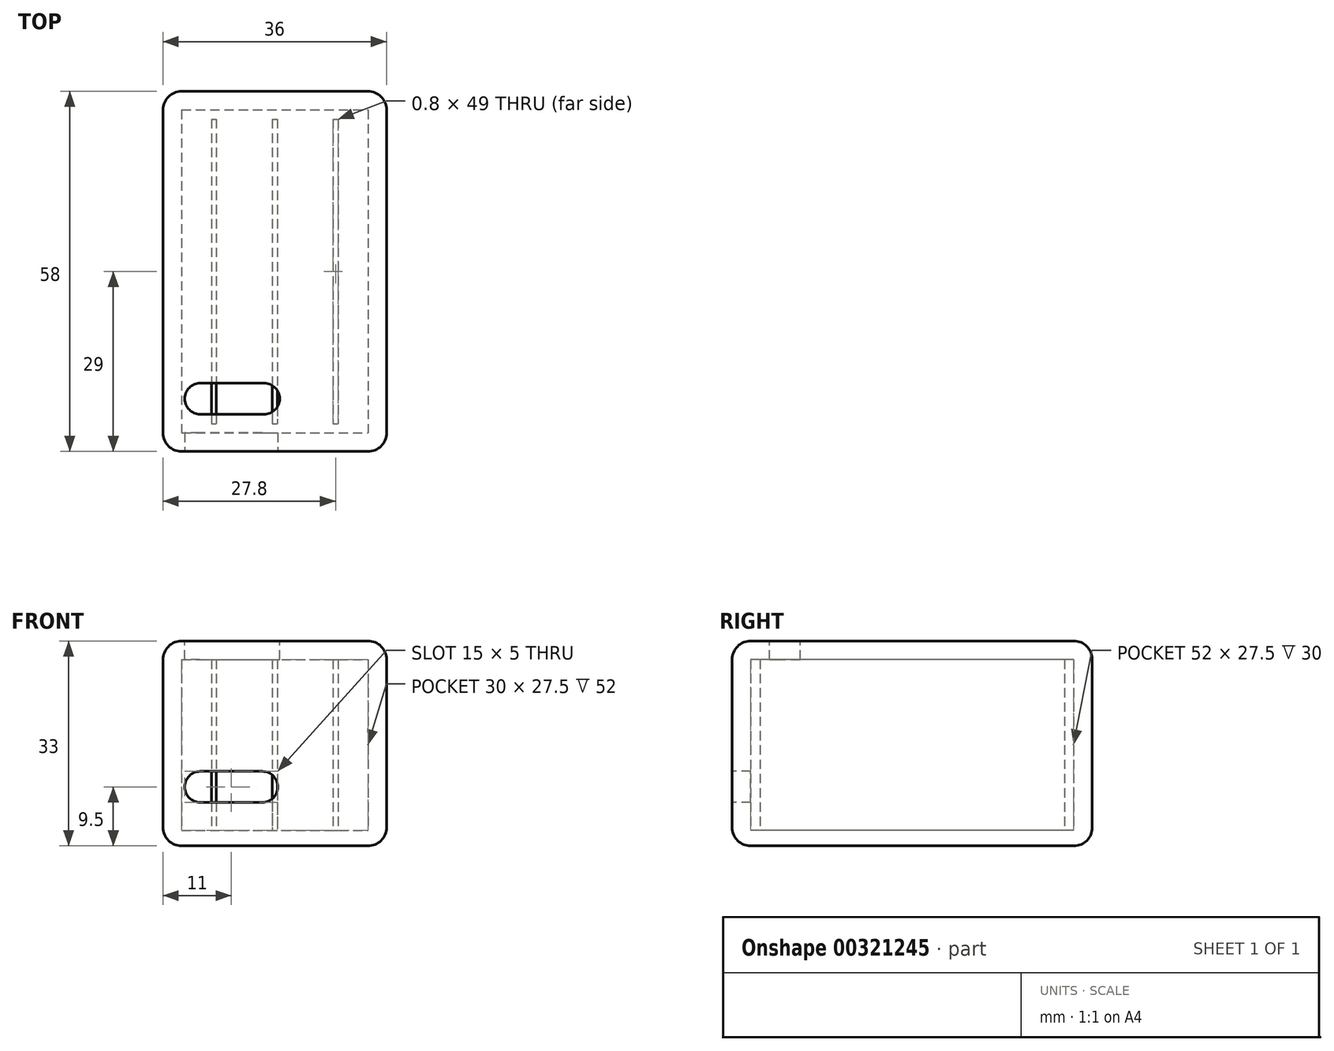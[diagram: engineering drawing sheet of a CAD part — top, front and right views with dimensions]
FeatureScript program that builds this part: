
annotation { "Feature Type Name" : "Feature", "Feature Type Description" : "" }
export const myFeature = defineFeature(function(context is Context, id is Id, definition is map)
    precondition{}
    {
        {
            var Q0;
            Q0=qCreatedBy(makeId("Top.planeOp"),FACE);
            var sketch = newSketch(context, id + "F0", { "sketchPlane" : qUnion([Q0])});
            skLineSegment(sketch, "E0.bottom", {"start": v(-15, 26) * mm, "end": v(15, 26) * mm});
            skLineSegment(sketch, "E0.top", {"start": v(-15, -26) * mm, "end": v(15, -26) * mm});
            skLineSegment(sketch, "E0.left", {"start": v(-15, 26) * mm, "end": v(-15, -26) * mm});
            skLineSegment(sketch, "E0.right", {"start": v(15, 26) * mm, "end": v(15, -26) * mm});
            skPoint(sketch, "E1", {"position": v(-15, 0) * mm});
            skPoint(sketch, "E2", {"position": v(0, 26) * mm});
            skLineSegment(sketch, "E3.bottom", {"start": v(-18, 29) * mm, "end": v(18, 29) * mm});
            skLineSegment(sketch, "E3.top", {"start": v(-18, -29) * mm, "end": v(18, -29) * mm});
            skLineSegment(sketch, "E3.left", {"start": v(-18, 29) * mm, "end": v(-18, -29) * mm});
            skLineSegment(sketch, "E3.right", {"start": v(18, 29) * mm, "end": v(18, -29) * mm});
            skPoint(sketch, "E4", {"position": v(-18, 0) * mm});
            skPoint(sketch, "E5", {"position": v(0, 29) * mm});
            skSolve(sketch);
        }
        {
            var Q0;
            Q0 = qSketchRegion(id + "F0", true);
            extrude(context, id + "F1", {"entities" : qUnion([Q0]), "depth" : 30 * mm});
        }
        {
            var Q0;
            Q0=makeQuery(id+"F0.imprint","IMPRINT",FACE,{"disambiguationData":[TD([[makeQuery(id+"F0.imprint","IMPRINT",EDGE,{"derivedFrom":sQuery(id+"F0.wireOp",EDGE,"E0.bottom")}),-1.0]])]});
            extrude(context, id + "F2", {"entities" : qUnion([Q0]), "operationType" : NewBodyOperationType.ADD, "depth" : 2.5 * mm});
        }
        {
            var Q0;
            Q0=makeQuery(id+"F1.opExtrude","SWEPT_FACE",FACE,{"disambiguationData":[OSD([sQuery(id+"F0.wireOp",EDGE,"E3.top")])]});
            var sketch = newSketch(context, id + "F3", { "sketchPlane" : qUnion([Q0])});
            skLineSegment(sketch, "E6.bottom", {"start": v(-12, 12) * mm, "end": v(-2, 12) * mm});
            skLineSegment(sketch, "E6.top", {"start": v(-12, 7) * mm, "end": v(-2, 7) * mm});
            skLineSegment(sketch, "E6.left", {"start": v(-12, 12) * mm, "end": v(-12, 7) * mm});
            skLineSegment(sketch, "E6.right", {"start": v(-2, 12) * mm, "end": v(-2, 7) * mm});
            skArc(sketch, "E7", {"start": v(-12, 12) * mm, "mid": v(-14.5, 9.5) * mm, "end": v(-12, 7) * mm});
            skArc(sketch, "E8", {"start": v(-2, 7) * mm, "mid": v(0.5, 9.5) * mm, "end": v(-2, 12) * mm});
            skSolve(sketch);
        }
        {
            var Q0;
            Q0 = qSketchRegion(id + "F3", true);
            extrude(context, id + "F4", {"entities" : qUnion([Q0]), "operationType" : NewBodyOperationType.REMOVE, "oppositeDirection" : true, "depth" : 25 * mm});
        }
        {
            var Q0;
            Q0=makeQuery(id+"F0.imprint","IMPRINT",FACE,{"disambiguationData":[TD([[makeQuery(id+"F0.imprint","IMPRINT",EDGE,{"derivedFrom":sQuery(id+"F0.wireOp",EDGE,"E0.bottom")}),-1.0]])]});
            var Q1;
            Q1=makeQuery(id+"F0.imprint","IMPRINT",FACE,{"disambiguationData":[TD([[makeQuery(id+"F0.imprint","IMPRINT",EDGE,{"derivedFrom":sQuery(id+"F0.wireOp",EDGE,"E0.bottom")}),1.0]])]});
            extrude(context, id + "F5", {"entities" : qUnion([Q0, Q1]), "depth" : 33 * mm, "hasSecondDirection" : true, "secondDirectionOppositeDirection" : false, "secondDirectionDepth" : 30 * mm});
        }
        {
            var Q0;
            {var subQ0=sQuery(id+"F0.wireOp",EDGE,"E0.right");var subQ1=sQuery(id+"F0.wireOp",EDGE,"E0.left");var subQ2=sQuery(id+"F0.wireOp",EDGE,"E0.top");var subQ3=sQuery(id+"F0.wireOp",EDGE,"E0.bottom");Q0=makeQuery(id+"F2.boolean.opBoolean","MERGE",FACE,{"derivedFrom":[makeQuery(id+"F1.opExtrude","CAP_FACE",FACE,{"disambiguationData":[OSD([subQ3,subQ2,subQ1,subQ0,sQuery(id+"F0.wireOp",EDGE,"E3.bottom"),sQuery(id+"F0.wireOp",EDGE,"E3.top"),sQuery(id+"F0.wireOp",EDGE,"E3.left"),sQuery(id+"F0.wireOp",EDGE,"E3.right")])],"isStart":true}),makeQuery(id+"F2.opExtrude","CAP_FACE",FACE,{"disambiguationData":[OSD([subQ3,subQ2,subQ1,subQ0])],"isStart":true})]});}
            var Q1;
            Q1=makeQuery(id+"F1.opExtrude","SWEPT_EDGE",EDGE,{"disambiguationData":[OSD([sQuery(id+"F0.wireOp",EDGE,"E3.top"),sQuery(id+"F0.wireOp",EDGE,"E3.left")])]});
            var Q2;
            Q2=makeQuery(id+"F1.opExtrude","SWEPT_EDGE",EDGE,{"disambiguationData":[OSD([sQuery(id+"F0.wireOp",EDGE,"E3.top"),sQuery(id+"F0.wireOp",EDGE,"E3.right")])]});
            var Q3;
            Q3=makeQuery(id+"F1.opExtrude","SWEPT_EDGE",EDGE,{"disambiguationData":[OSD([sQuery(id+"F0.wireOp",EDGE,"E3.bottom"),sQuery(id+"F0.wireOp",EDGE,"E3.right")])]});
            var Q4;
            Q4=makeQuery(id+"F1.opExtrude","SWEPT_EDGE",EDGE,{"disambiguationData":[OSD([sQuery(id+"F0.wireOp",EDGE,"E3.bottom"),sQuery(id+"F0.wireOp",EDGE,"E3.left")])]});
            var Q5;
            Q5=makeQuery(id+"F5.opExtrude","SWEPT_EDGE",EDGE,{"disambiguationData":[OSD([sQuery(id+"F0.wireOp",EDGE,"E3.top"),sQuery(id+"F0.wireOp",EDGE,"E3.left")])]});
            var Q6;
            Q6=makeQuery(id+"F5.opExtrude","CAP_FACE",FACE,{"disambiguationData":[OSD([sQuery(id+"F0.wireOp",EDGE,"E3.bottom"),sQuery(id+"F0.wireOp",EDGE,"E3.top"),sQuery(id+"F0.wireOp",EDGE,"E3.left"),sQuery(id+"F0.wireOp",EDGE,"E3.right")])],"isStart":false});
            var Q7;
            Q7=makeQuery(id+"F5.opExtrude","SWEPT_EDGE",EDGE,{"disambiguationData":[OSD([sQuery(id+"F0.wireOp",EDGE,"E3.top"),sQuery(id+"F0.wireOp",EDGE,"E3.right")])]});
            var Q8;
            Q8=makeQuery(id+"F5.opExtrude","SWEPT_EDGE",EDGE,{"disambiguationData":[OSD([sQuery(id+"F0.wireOp",EDGE,"E3.bottom"),sQuery(id+"F0.wireOp",EDGE,"E3.right")])]});
            var Q9;
            Q9=makeQuery(id+"F5.opExtrude","SWEPT_EDGE",EDGE,{"disambiguationData":[OSD([sQuery(id+"F0.wireOp",EDGE,"E3.bottom"),sQuery(id+"F0.wireOp",EDGE,"E3.left")])]});
            fillet(context, id + "F6", {"entities" : qUnion([Q0, Q1, Q2, Q3, Q4, Q5, Q6, Q7, Q8, Q9]), "radius" : 3 * mm, "tangentPropagation" : true, "allowEdgeOverflow" : false});
        }
        {
            var Q0;
            Q0=makeQuery(id+"F5.opExtrude","CAP_FACE",FACE,{"disambiguationData":[OSD([sQuery(id+"F0.wireOp",EDGE,"E3.bottom"),sQuery(id+"F0.wireOp",EDGE,"E3.top"),sQuery(id+"F0.wireOp",EDGE,"E3.left"),sQuery(id+"F0.wireOp",EDGE,"E3.right")])],"isStart":false});
            var sketch = newSketch(context, id + "F7", { "sketchPlane" : qUnion([Q0])});
            skLineSegment(sketch, "E9.bottom", {"start": v(-12, -18) * mm, "end": v(-1.71, -18) * mm});
            skLineSegment(sketch, "E9.top", {"start": v(-12, -23) * mm, "end": v(-1.71, -23) * mm});
            skLineSegment(sketch, "E9.left", {"start": v(-12, -18) * mm, "end": v(-12, -23) * mm});
            skLineSegment(sketch, "E9.right", {"start": v(-1.71, -18) * mm, "end": v(-1.71, -23) * mm});
            skArc(sketch, "E10", {"start": v(-12, -18) * mm, "mid": v(-14.5, -20.5) * mm, "end": v(-12, -23) * mm});
            skArc(sketch, "E11", {"start": v(-1.71, -23) * mm, "mid": v(0.79, -20.5) * mm, "end": v(-1.71, -18) * mm});
            skSolve(sketch);
        }
        {
            var Q0;
            Q0 = qSketchRegion(id + "F7", true);
            extrude(context, id + "F8", {"entities" : qUnion([Q0]), "operationType" : NewBodyOperationType.REMOVE, "oppositeDirection" : true, "depth" : 3 * mm});
        }
        {
            var Q0;
            Q0=makeQuery(id+"F2.opExtrude","CAP_FACE",FACE,{"disambiguationData":[OSD([sQuery(id+"F0.wireOp",EDGE,"E0.bottom"),sQuery(id+"F0.wireOp",EDGE,"E0.top"),sQuery(id+"F0.wireOp",EDGE,"E0.left"),sQuery(id+"F0.wireOp",EDGE,"E0.right")])],"isStart":false});
            var sketch = newSketch(context, id + "F9", { "sketchPlane" : qUnion([Q0])});
            skLineSegment(sketch, "E12.bottom", {"start": v(-10.2, 24.5) * mm, "end": v(-9.4, 24.5) * mm});
            skLineSegment(sketch, "E12.top", {"start": v(-10.2, -24.5) * mm, "end": v(-9.4, -24.5) * mm});
            skLineSegment(sketch, "E12.left", {"start": v(-10.2, 24.5) * mm, "end": v(-10.2, -24.5) * mm});
            skLineSegment(sketch, "E12.right", {"start": v(-9.4, 24.5) * mm, "end": v(-9.4, -24.5) * mm});
            skLineSegment(sketch, "E13.bottom", {"start": v(-0.4, 24.5) * mm, "end": v(0.4, 24.5) * mm});
            skLineSegment(sketch, "E13.top", {"start": v(-0.4, -24.5) * mm, "end": v(0.4, -24.5) * mm});
            skLineSegment(sketch, "E13.left", {"start": v(-0.4, 24.5) * mm, "end": v(-0.4, -24.5) * mm});
            skLineSegment(sketch, "E13.right", {"start": v(0.4, 24.5) * mm, "end": v(0.4, -24.5) * mm});
            skLineSegment(sketch, "E14.bottom", {"start": v(9.4, 24.5) * mm, "end": v(10.2, 24.5) * mm});
            skLineSegment(sketch, "E14.top", {"start": v(9.4, -24.5) * mm, "end": v(10.2, -24.5) * mm});
            skLineSegment(sketch, "E14.left", {"start": v(9.4, 24.5) * mm, "end": v(9.4, -24.5) * mm});
            skLineSegment(sketch, "E14.right", {"start": v(10.2, 24.5) * mm, "end": v(10.2, -24.5) * mm});
            skSolve(sketch);
        }
        {
            var Q0;
            Q0 = qSketchRegion(id + "F9", true);
            extrude(context, id + "F10", {"entities" : qUnion([Q0]), "operationType" : NewBodyOperationType.ADD, "depth" : 27.5 * mm});
        }
    });
